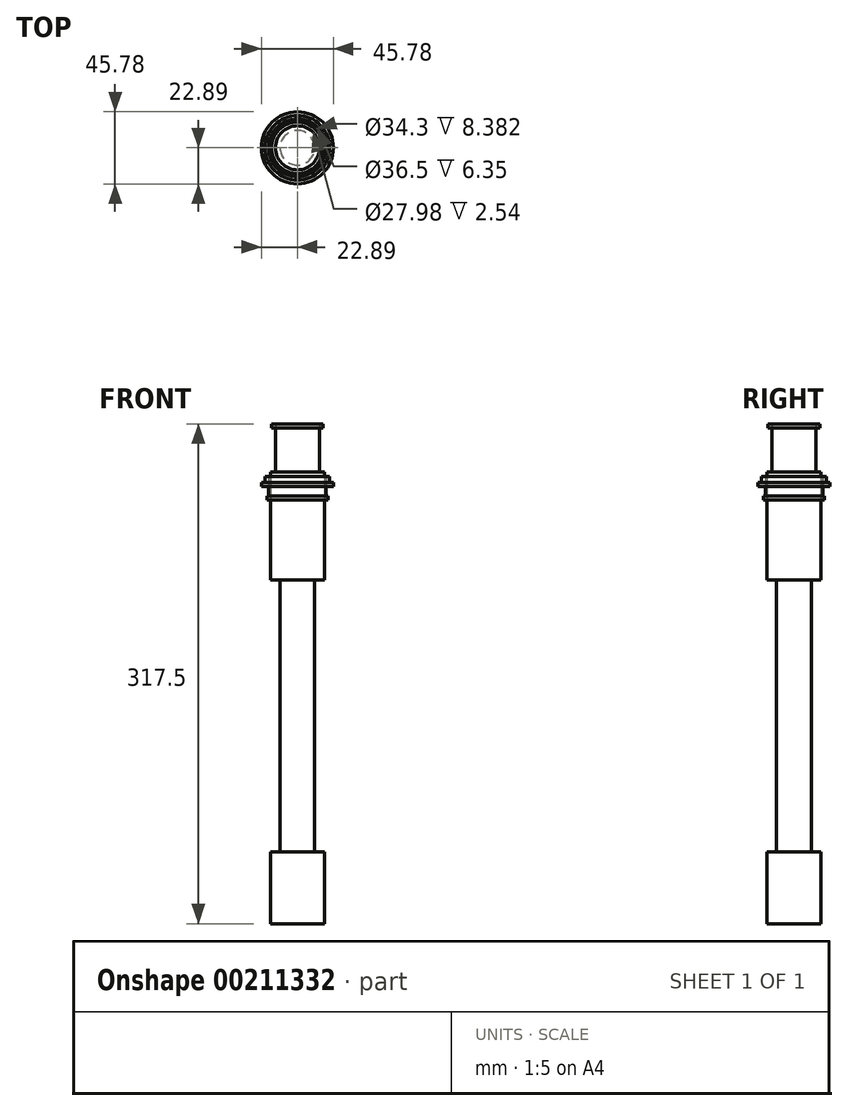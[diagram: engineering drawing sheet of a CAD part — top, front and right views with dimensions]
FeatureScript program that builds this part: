
annotation { "Feature Type Name" : "Feature", "Feature Type Description" : "" }
export const myFeature = defineFeature(function(context is Context, id is Id, definition is map)
    precondition{}
    {
        {
            var Q0;
            Q0=qCreatedBy(makeId("Top.planeOp"),FACE);
            var sketch = newSketch(context, id + "F0", { "sketchPlane" : qUnion([Q0])});
            skCircle(sketch, "E0", {"center": v(0, 0) * mm, "radius": 17.08 * mm});
            skSolve(sketch);
        }
        {
            var Q0;
            Q0=makeQuery(id+"F0.imprint","IMPRINT",FACE,{"disambiguationData":[TD([[makeQuery(id+"F0.imprint","IMPRINT",EDGE,{"derivedFrom":sQuery(id+"F0.wireOp",EDGE,"E0")}),1.0]])]});
            extrude(context, id + "F1", {"entities" : qUnion([Q0]), "depth" : 45.72 * mm});
        }
        {
            var Q0;
            Q0=makeQuery(id+"F1.opExtrude","CAP_FACE",FACE,{"disambiguationData":[OSD([sQuery(id+"F0.wireOp",EDGE,"E0")])],"isStart":false});
            var sketch = newSketch(context, id + "F2", { "sketchPlane" : qUnion([Q0])});
            skCircle(sketch, "E1", {"center": v(0, 0) * mm, "radius": 11 * mm});
            skSolve(sketch);
        }
        {
            var Q0;
            Q0 = qSketchRegion(id + "F2", true);
            extrude(context, id + "F3", {"entities" : qUnion([Q0]), "operationType" : NewBodyOperationType.ADD, "depth" : 172.72 * mm});
        }
        {
            var Q0;
            Q0=qCreatedBy(makeId("Top.planeOp"),FACE);
            cPlane(context, id + "F4", {"entities" : qUnion([Q0]), "cplaneType" : CPlaneType.OFFSET, "offset" : 218.44 * mm, "width" : 152.4 * mm, "height" : 152.4 * mm});
        }
        {
            var Q0;
            Q0=qCreatedBy(id+"F4.planeOp",FACE);
            var sketch = newSketch(context, id + "F5", { "sketchPlane" : qUnion([Q0])});
            skCircle(sketch, "E2", {"center": v(0, 0) * mm, "radius": 17.15 * mm});
            skSolve(sketch);
        }
        {
            var Q0;
            Q0=makeQuery(id+"F5.imprint","IMPRINT",FACE,{"disambiguationData":[TD([[makeQuery(id+"F5.imprint","IMPRINT",EDGE,{"derivedFrom":sQuery(id+"F5.wireOp",EDGE,"E2")}),1.0]])]});
            extrude(context, id + "F6", {"entities" : qUnion([Q0]), "operationType" : NewBodyOperationType.ADD, "depth" : 50.8 * mm});
        }
        {
            var Q0;
            Q0=makeQuery(id+"F6.opExtrude","CAP_FACE",FACE,{"disambiguationData":[OSD([sQuery(id+"F5.wireOp",EDGE,"E2")])],"isStart":false});
            var sketch = newSketch(context, id + "F7", { "sketchPlane" : qUnion([Q0])});
            skCircle(sketch, "E3", {"center": v(0, 0) * mm, "radius": 19.44 * mm});
            skSolve(sketch);
        }
        {
            var Q0;
            Q0=makeQuery(id+"F7.imprint","IMPRINT",FACE,{"disambiguationData":[TD([[makeQuery(id+"F7.imprint","IMPRINT",EDGE,{"derivedFrom":sQuery(id+"F7.wireOp",EDGE,"E3")}),1.0]])]});
            extrude(context, id + "F8", {"entities" : qUnion([Q0]), "depth" : 2.54 * mm});
        }
        {
            var Q0;
            Q0=makeQuery(id+"F8.opExtrude","CAP_FACE",FACE,{"disambiguationData":[OSD([sQuery(id+"F5.wireOp",EDGE,"E2"),sQuery(id+"F7.wireOp",EDGE,"E3")])],"isStart":false});
            var sketch = newSketch(context, id + "F9", { "sketchPlane" : qUnion([Q0])});
            skCircle(sketch, "E4", {"center": v(0, 0) * mm, "radius": 18.25 * mm});
            skSolve(sketch);
        }
        {
            var Q0;
            Q0=makeQuery(id+"F9.imprint","IMPRINT",FACE,{"disambiguationData":[TD([[makeQuery(id+"F9.imprint","IMPRINT",EDGE,{"derivedFrom":sQuery(id+"F9.wireOp",EDGE,"E4")}),1.0]])]});
            extrude(context, id + "F10", {"entities" : qUnion([Q0]), "operationType" : NewBodyOperationType.ADD, "depth" : 5.84 * mm});
        }
        {
            var Q0;
            Q0=makeQuery(id+"F10.opExtrude","CAP_FACE",FACE,{"disambiguationData":[OSD([sQuery(id+"F5.wireOp",EDGE,"E2"),sQuery(id+"F9.wireOp",EDGE,"E4")])],"isStart":false});
            var sketch = newSketch(context, id + "F11", { "sketchPlane" : qUnion([Q0])});
            skCircle(sketch, "E5", {"center": v(0, 0) * mm, "radius": 22.9 * mm});
            skSolve(sketch);
        }
        {
            var Q0;
            Q0=makeQuery(id+"F11.imprint","IMPRINT",FACE,{"disambiguationData":[TD([[makeQuery(id+"F11.imprint","IMPRINT",EDGE,{"derivedFrom":sQuery(id+"F11.wireOp",EDGE,"E5")}),1.0]])]});
            extrude(context, id + "F12", {"entities" : qUnion([Q0]), "depth" : 2.54 * mm});
        }
        {
            var Q0;
            Q0=makeQuery(id+"F12.opExtrude","CAP_FACE",FACE,{"disambiguationData":[OSD([sQuery(id+"F9.wireOp",EDGE,"E4"),sQuery(id+"F11.wireOp",EDGE,"E5")])],"isStart":false});
            var sketch = newSketch(context, id + "F13", { "sketchPlane" : qUnion([Q0])});
            skCircle(sketch, "E6", {"center": v(0, 0) * mm, "radius": 20.55 * mm});
            skSolve(sketch);
        }
        {
            var Q0;
            Q0=makeQuery(id+"F13.imprint","IMPRINT",FACE,{"disambiguationData":[TD([[makeQuery(id+"F13.imprint","IMPRINT",EDGE,{"derivedFrom":sQuery(id+"F13.wireOp",EDGE,"E6")}),1.0]])]});
            extrude(context, id + "F14", {"entities" : qUnion([Q0]), "operationType" : NewBodyOperationType.ADD, "depth" : 3.8 * mm});
        }
        {
            var Q0;
            Q0=makeQuery(id+"F6.opExtrude","CAP_FACE",FACE,{"disambiguationData":[OSD([sQuery(id+"F5.wireOp",EDGE,"E2")])],"isStart":false});
            extrude(context, id + "F15", {"entities" : qUnion([Q0]), "depth" : 17.78 * mm});
        }
        {
            var Q0;
            Q0=makeQuery(id+"F15.opExtrude","CAP_FACE",FACE,{"disambiguationData":[OSD([sQuery(id+"F5.wireOp",EDGE,"E2")])],"isStart":false});
            var sketch = newSketch(context, id + "F16", { "sketchPlane" : qUnion([Q0])});
            skCircle(sketch, "E7", {"center": v(0, 0) * mm, "radius": 17.46 * mm});
            skSolve(sketch);
        }
        {
            var Q0;
            Q0=makeQuery(id+"F16.imprint","IMPRINT",FACE,{"disambiguationData":[TD([[makeQuery(id+"F16.imprint","IMPRINT",EDGE,{"derivedFrom":makeQuery(id+"F15.opExtrude","CAP_EDGE",EDGE,{"disambiguationData":[OSD([sQuery(id+"F5.wireOp",EDGE,"E2")])],"isStart":false})}),1.0]])]});
            var sketch = newSketch(context, id + "F17", { "sketchPlane" : qUnion([Q0])});
            skCircle(sketch, "E8", {"center": v(0, 0) * mm, "radius": 14 * mm});
            skSolve(sketch);
        }
        {
            var Q0;
            Q0=makeQuery(id+"F17.imprint","IMPRINT",FACE,{"disambiguationData":[TD([[makeQuery(id+"F17.imprint","IMPRINT",EDGE,{"derivedFrom":sQuery(id+"F17.wireOp",EDGE,"E8")}),1.0]])]});
            extrude(context, id + "F18", {"entities" : qUnion([Q0]), "operationType" : NewBodyOperationType.ADD, "depth" : 27.94 * mm});
        }
        {
            var Q0;
            Q0=makeQuery(id+"F18.opExtrude","CAP_FACE",FACE,{"disambiguationData":[OSD([sQuery(id+"F17.wireOp",EDGE,"E8")])],"isStart":false});
            var sketch = newSketch(context, id + "F19", { "sketchPlane" : qUnion([Q0])});
            skCircle(sketch, "E9", {"center": v(0, 0) * mm, "radius": 16.38 * mm});
            skSolve(sketch);
        }
        {
            var Q0;
            Q0=makeQuery(id+"F19.imprint","IMPRINT",FACE,{"disambiguationData":[TD([[makeQuery(id+"F19.imprint","IMPRINT",EDGE,{"derivedFrom":sQuery(id+"F19.wireOp",EDGE,"E9")}),1.0]])]});
            extrude(context, id + "F20", {"entities" : qUnion([Q0]), "depth" : 2.54 * mm});
        }
    });
